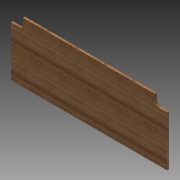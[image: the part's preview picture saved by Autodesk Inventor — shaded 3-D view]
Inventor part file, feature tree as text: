
AUTODESK INVENTOR PART (.ipt)
format: ipt  version: 2012 (Build 160160000, 160)  size: 103,424 bytes
history: native  units: in
note: dims shown in document units (in); Inventor stores cm internally (conversion verified against a paired STEP export)
features: extrude x1, sketch x1
ambient origin geometry x8: Origin, YZ Plane, XZ Plane, XY Plane, X Axis, Y Axis, Z Axis, Center Point
bodies: Solid1 (feature_tree)
feature tree (2):
  extrude  "Extrusion1"  Depth=19.5in
  sketch  "Sketch1"  dims[d0=7.5in d1=19.5in d2=0.25in d3=0.0in d4=1.0in d5=1.0in d6=1.0in d7=0.75in d8=1.0in d9=0.75in]
